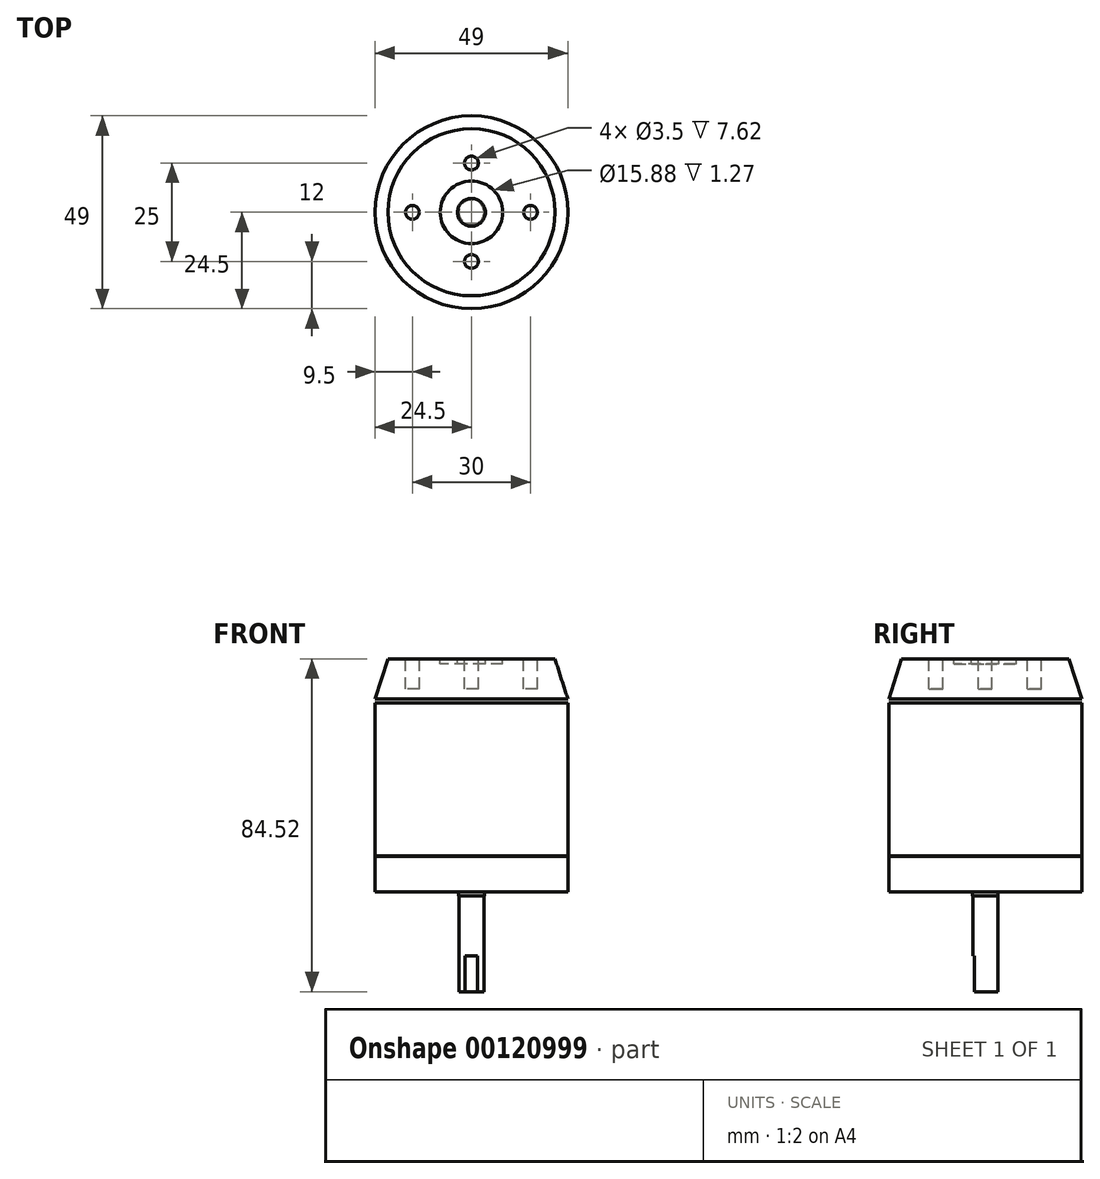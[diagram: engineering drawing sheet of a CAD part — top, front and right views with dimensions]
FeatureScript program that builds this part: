
annotation { "Feature Type Name" : "Feature", "Feature Type Description" : "" }
export const myFeature = defineFeature(function(context is Context, id is Id, definition is map)
    precondition{}
    {
        {
            var Q0;
            Q0=qCreatedBy(makeId("Top.planeOp"),FACE);
            var sketch = newSketch(context, id + "F0", { "sketchPlane" : qUnion([Q0])});
            skCircle(sketch, "E0", {"center": v(0, 0) * mm, "radius": 24.5 * mm});
            skSolve(sketch);
        }
        {
            var Q0;
            Q0=qSketchRegion(id+"F0",true);
            extrude(context, id + "F1", {"entities" : qUnion([Q0]), "depth" : 38.8 * mm});
        }
        {
            var Q0;
            Q0=makeQuery(id+"F1.opExtrude","CAP_FACE",FACE,{"disambiguationData":[OSD([sQuery(id+"F0.wireOp",EDGE,"E0")])],"isStart":true});
            cPlane(context, id + "F2", {"entities" : qUnion([Q0]), "cplaneType" : CPlaneType.OFFSET, "offset" : 0.1 * mm, "width" : 152.4 * mm, "height" : 152.4 * mm});
        }
        {
            var Q0;
            Q0=qCreatedBy(id+"F2.planeOp",FACE);
            var sketch = newSketch(context, id + "F3", { "sketchPlane" : qUnion([Q0])});
            skCircle(sketch, "E1", {"center": v(0, 0) * mm, "radius": 24.5 * mm});
            skSolve(sketch);
        }
        {
            var Q0;
            Q0=qSketchRegion(id+"F3",true);
            extrude(context, id + "F4", {"entities" : qUnion([Q0]), "depth" : 9 * mm});
        }
        {
            var Q0;
            Q0=makeQuery(id+"F1.opExtrude","CAP_FACE",FACE,{"disambiguationData":[OSD([sQuery(id+"F0.wireOp",EDGE,"E0")])],"isStart":false});
            cPlane(context, id + "F5", {"entities" : qUnion([Q0]), "cplaneType" : CPlaneType.OFFSET, "offset" : 1.02 * mm, "width" : 152.4 * mm, "height" : 152.4 * mm});
        }
        {
            var Q0;
            Q0=qCreatedBy(id+"F5.planeOp",FACE);
            var sketch = newSketch(context, id + "F6", { "sketchPlane" : qUnion([Q0])});
            skCircle(sketch, "E2", {"center": v(0, 0) * mm, "radius": 24.5 * mm});
            skSolve(sketch);
        }
        {
            var Q0;
            Q0=qCreatedBy(id+"F5.planeOp",FACE);
            cPlane(context, id + "F7", {"entities" : qUnion([Q0]), "cplaneType" : CPlaneType.OFFSET, "offset" : 10.2 * mm, "width" : 152.4 * mm, "height" : 152.4 * mm});
        }
        {
            var Q0;
            Q0=qCreatedBy(id+"F7.planeOp",FACE);
            var sketch = newSketch(context, id + "F8", { "sketchPlane" : qUnion([Q0])});
            skCircle(sketch, "E3", {"center": v(0, 0) * mm, "radius": 21.22 * mm});
            skSolve(sketch);
        }
        {
            var Q0;
            Q0=makeQuery(id+"F6.imprint","IMPRINT",FACE,{"disambiguationData":[TD([[makeQuery(id+"F6.imprint","IMPRINT",EDGE,{"derivedFrom":sQuery(id+"F6.wireOp",EDGE,"E2")}),1.0]])]});
            var Q1;
            Q1=makeQuery(id+"F8.imprint","IMPRINT",FACE,{"disambiguationData":[TD([[makeQuery(id+"F8.imprint","IMPRINT",EDGE,{"derivedFrom":sQuery(id+"F8.wireOp",EDGE,"E3")}),1.0]])]});
            loft(context, id + "F9", {"sheetProfilesArray" : [{ "sheetProfileEntities" : qUnion([Q0]) }, { "sheetProfileEntities" : qUnion([Q1]) }]});
        }
        {
            var Q0;
            Q0=makeQuery(id+"F9.opLoft","CAP_FACE",FACE,{"disambiguationData":[OSD([makeQuery(id+"F8.imprint","IMPRINT",FACE,{"disambiguationData":[TD([[makeQuery(id+"F8.imprint","IMPRINT",EDGE,{"derivedFrom":sQuery(id+"F8.wireOp",EDGE,"E3")}),1.0]])]})])],"isStart":true});
            var sketch = newSketch(context, id + "F10", { "sketchPlane" : qUnion([Q0])});
            skCircle(sketch, "E4", {"center": v(0, 0) * mm, "radius": 3.53 * mm});
            skCircle(sketch, "E5", {"center": v(0, 0) * mm, "radius": 7.94 * mm});
            skSolve(sketch);
        }
        {
            var Q0;
            Q0=qSketchRegion(id+"F10",true);
            extrude(context, id + "F11", {"entities" : qUnion([Q0]), "operationType" : NewBodyOperationType.REMOVE, "oppositeDirection" : true, "depth" : 1.27 * mm});
        }
        {
            var Q0;
            Q0=makeQuery(id+"F9.opLoft","CAP_FACE",FACE,{"disambiguationData":[OSD([makeQuery(id+"F8.imprint","IMPRINT",FACE,{"disambiguationData":[TD([[makeQuery(id+"F8.imprint","IMPRINT",EDGE,{"derivedFrom":sQuery(id+"F8.wireOp",EDGE,"E3")}),1.0]])]})])],"isStart":true});
            var sketch = newSketch(context, id + "F12", { "sketchPlane" : qUnion([Q0])});
            skCircle(sketch, "E6", {"center": v(0, 12.5) * mm, "radius": 1.75 * mm});
            skCircle(sketch, "E7", {"center": v(0, -12.5) * mm, "radius": 1.75 * mm});
            skCircle(sketch, "E8", {"center": v(15, 0) * mm, "radius": 1.75 * mm});
            skCircle(sketch, "E9", {"center": v(-15, 0) * mm, "radius": 1.75 * mm});
            skLineSegment(sketch, "E10", {"start": v(0, 12.5) * mm, "end": v(0, -12.5) * mm, "construction": true});
            skLineSegment(sketch, "E11", {"start": v(-15, 0) * mm, "end": v(15, 0) * mm, "construction": true});
            skSolve(sketch);
        }
        {
            var Q0;
            Q0=qSketchRegion(id+"F12",true);
            extrude(context, id + "F13", {"entities" : qUnion([Q0]), "operationType" : NewBodyOperationType.REMOVE, "oppositeDirection" : true, "depth" : 7.62 * mm});
        }
        {
            var Q0;
            Q0=qCreatedBy(makeId("Right.planeOp"),FACE);
            var sketch = newSketch(context, id + "F14", { "sketchPlane" : qUnion([Q0])});
            skLineSegment(sketch, "E12", {"start": v(0, -9.1) * mm, "end": v(0, -34.5) * mm});
            skLineSegment(sketch, "E13", {"start": v(0, -34.5) * mm, "end": v(3.18, -34.5) * mm});
            skLineSegment(sketch, "E14", {"start": v(3.18, -34.5) * mm, "end": v(3.18, -10.1) * mm});
            skLineSegment(sketch, "E15", {"start": v(3.18, -10.1) * mm, "end": v(3.25, -10.1) * mm});
            skLineSegment(sketch, "E16", {"start": v(3.25, -10.1) * mm, "end": v(3.25, -9.1) * mm});
            skLineSegment(sketch, "E17", {"start": v(3.25, -9.1) * mm, "end": v(0, -9.1) * mm});
            skSolve(sketch);
        }
        {
            var Q0;
            Q0=qSketchRegion(id+"F14",true);
            var Q1;
            Q1=sQuery(id+"F14.wireOp",EDGE,"E12");
            revolve(context, id + "F15", {"operationType" : NewBodyOperationType.ADD, "entities" : qUnion([Q0]), "axis" : qUnion([Q1]), "revolveType" : RevolveType.FULL});
        }
        {
            var Q0;
            Q0=makeQuery(id+"F15.opRevolve","SWEPT_FACE",FACE,{"disambiguationData":[OSD([sQuery(id+"F14.wireOp",EDGE,"E13")])]});
            var sketch = newSketch(context, id + "F16", { "sketchPlane" : qUnion([Q0])});
            skLineSegment(sketch, "E18", {"start": v(-1.59, 2.75) * mm, "end": v(1.59, 2.75) * mm});
            skArc(sketch, "E19.0", {"start": v(1.59, 2.75) * mm, "mid": v(0, 3.18) * mm, "end": v(-1.59, 2.75) * mm});
            skSolve(sketch);
        }
        {
            var Q0;
            Q0=qSketchRegion(id+"F16",true);
            extrude(context, id + "F17", {"entities" : qUnion([Q0]), "operationType" : NewBodyOperationType.REMOVE, "oppositeDirection" : true, "depth" : 9.14 * mm});
        }
    });
